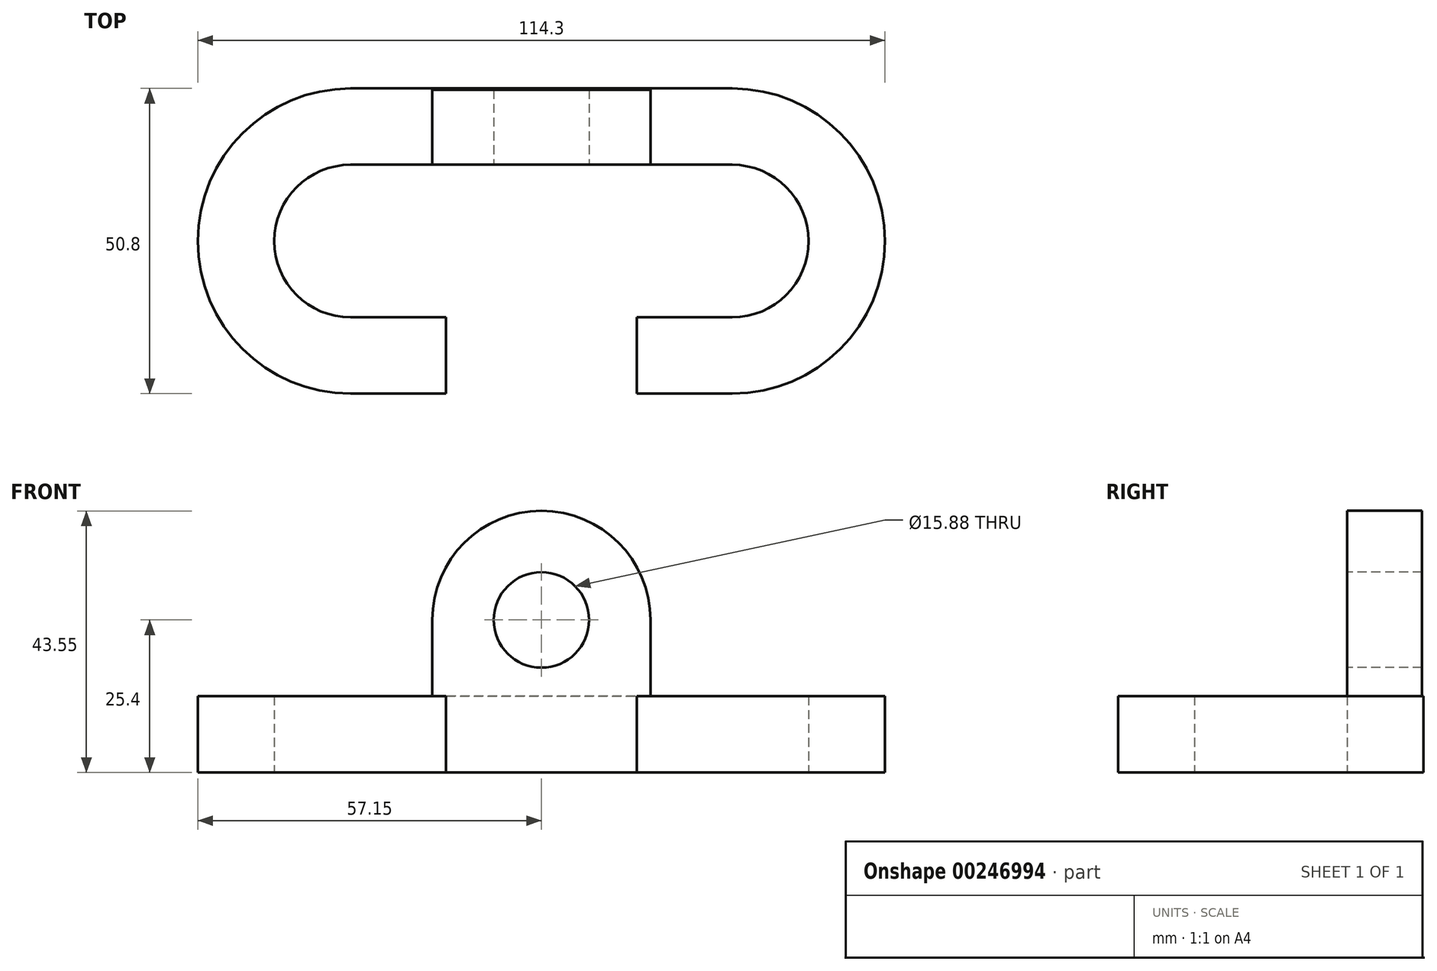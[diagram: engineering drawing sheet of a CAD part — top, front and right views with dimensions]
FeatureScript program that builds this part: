
annotation { "Feature Type Name" : "Feature", "Feature Type Description" : "" }
export const myFeature = defineFeature(function(context is Context, id is Id, definition is map)
    precondition{}
    {
        {
            var Q0;
            Q0=qCreatedBy(makeId("Top.planeOp"),FACE);
            var sketch = newSketch(context, id + "F0", { "sketchPlane" : qUnion([Q0])});
            skArc(sketch, "E0", {"start": v(31.75, -25.4) * mm, "mid": v(57.15, 0) * mm, "end": v(31.75, 25.4) * mm});
            skArc(sketch, "E1", {"start": v(31.75, -12.7) * mm, "mid": v(44.45, 0) * mm, "end": v(31.75, 12.7) * mm});
            skLineSegment(sketch, "E2", {"start": v(31.75, 25.4) * mm, "end": v(0, 25.4) * mm});
            skLineSegment(sketch, "E3", {"start": v(31.75, 12.7) * mm, "end": v(0, 12.7) * mm});
            skLineSegment(sketch, "E4", {"start": v(31.75, -12.7) * mm, "end": v(15.88, -12.7) * mm});
            skLineSegment(sketch, "E5", {"start": v(31.75, -25.4) * mm, "end": v(15.88, -25.4) * mm});
            skLineSegment(sketch, "E6", {"start": v(15.88, -25.4) * mm, "end": v(15.88, -12.7) * mm});
            skArc(sketch, "E7.MirrorCS", {"start": v(-31.75, -25.4) * mm, "mid": v(-57.15, 0) * mm, "end": v(-31.75, 25.4) * mm});
            skLineSegment(sketch, "E8.MirrorCS", {"start": v(-31.75, 25.4) * mm, "end": v(0, 25.4) * mm});
            skLineSegment(sketch, "E9.MirrorCS", {"start": v(-31.75, 12.7) * mm, "end": v(0, 12.7) * mm});
            skLineSegment(sketch, "E10.MirrorCS", {"start": v(-31.75, -12.7) * mm, "end": v(-15.88, -12.7) * mm});
            skLineSegment(sketch, "E11.MirrorCS", {"start": v(-15.88, -25.4) * mm, "end": v(-15.88, -12.7) * mm});
            skLineSegment(sketch, "E12.MirrorCS", {"start": v(-31.75, -25.4) * mm, "end": v(-15.88, -25.4) * mm});
            skArc(sketch, "E13.MirrorCS", {"start": v(-31.75, -12.7) * mm, "mid": v(-44.45, 0) * mm, "end": v(-31.75, 12.7) * mm});
            skSolve(sketch);
        }
        {
            var Q0;
            Q0=makeQuery(id+"F0.imprint","IMPRINT",FACE,{"disambiguationData":[TD([[makeQuery(id+"F0.imprint","IMPRINT",EDGE,{"derivedFrom":sQuery(id+"F0.wireOp",EDGE,"E0")}),1.0]])]});
            extrude(context, id + "F1", {"entities" : qUnion([Q0]), "depth" : 12.7 * mm});
        }
        {
            var Q0;
            Q0=makeQuery(id+"F1.opExtrude","SWEPT_FACE",FACE,{"disambiguationData":[OSD([sQuery(id+"F0.wireOp",EDGE,"E3"),sQuery(id+"F0.wireOp",EDGE,"E9.MirrorCS")])]});
            var sketch = newSketch(context, id + "F2", { "sketchPlane" : qUnion([Q0])});
            skCircle(sketch, "E14", {"center": v(0, 25.4) * mm, "radius": 7.94 * mm});
            skPoint(sketch, "E14.centerSnap0", {"position": v(0, 0) * mm});
            skArc(sketch, "E15", {"start": v(18.15, 25.4) * mm, "mid": v(0, 43.55) * mm, "end": v(-18.15, 25.4) * mm});
            skLineSegment(sketch, "E16", {"start": v(-18.15, 25.4) * mm, "end": v(-18.15, 12.7) * mm});
            skPoint(sketch, "E17.orphan", {"position": v(-7.94, 25.4) * mm});
            skLineSegment(sketch, "E18", {"start": v(18.15, 25.4) * mm, "end": v(18.15, 12.7) * mm});
            skSolve(sketch);
        }
        {
            var Q0;
            Q0=makeQuery(id+"F2.imprint","IMPRINT",FACE,{"disambiguationData":[TD([[makeQuery(id+"F2.imprint","IMPRINT",EDGE,{"derivedFrom":sQuery(id+"F2.wireOp",EDGE,"E14")}),-1.0]])]});
            extrude(context, id + "F3", {"entities" : qUnion([Q0]), "operationType" : NewBodyOperationType.ADD, "oppositeDirection" : true, "depth" : 12.45 * mm});
        }
    });
